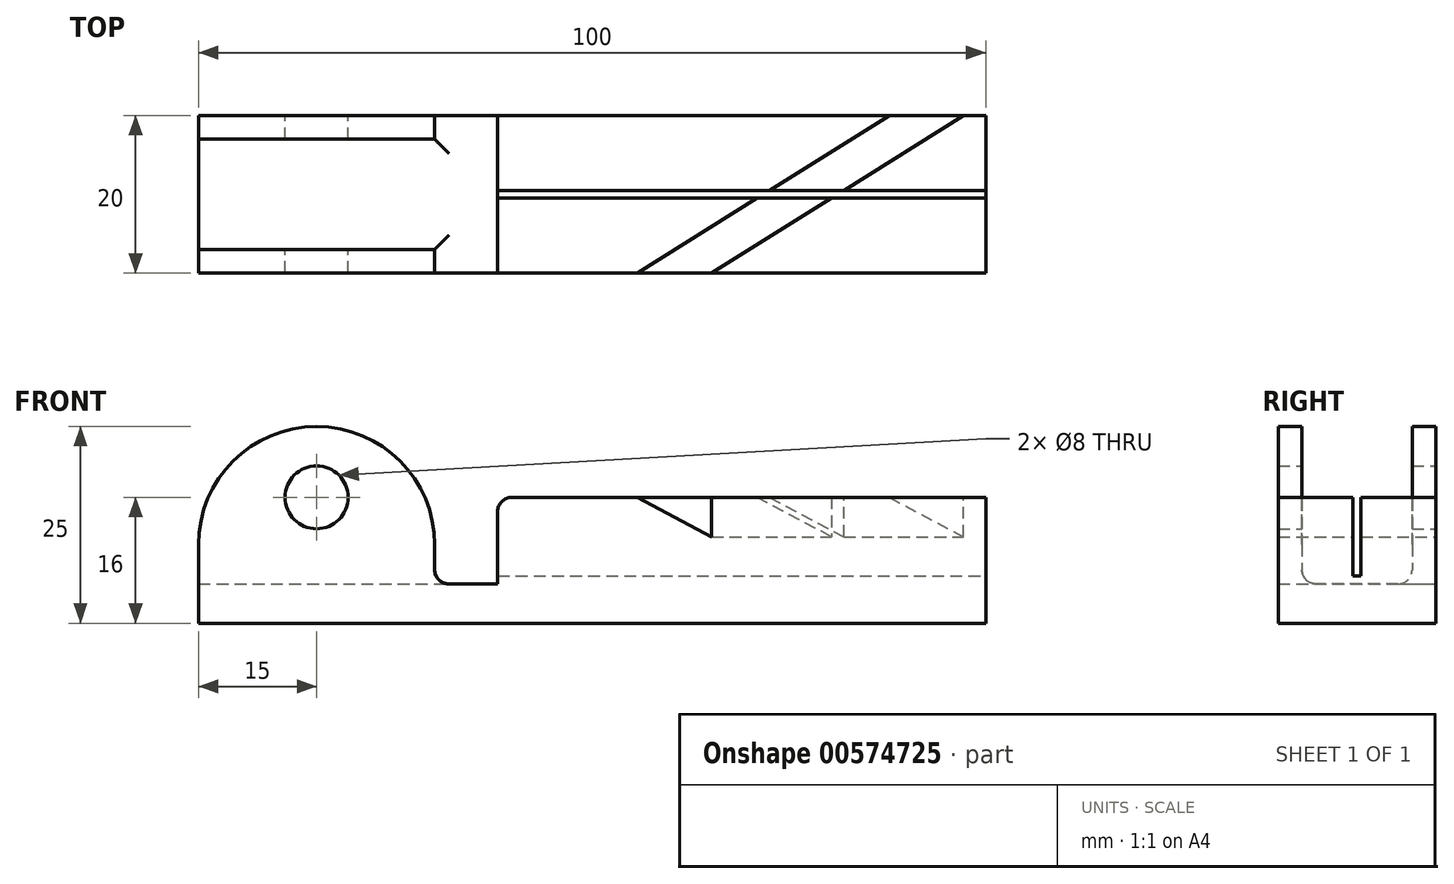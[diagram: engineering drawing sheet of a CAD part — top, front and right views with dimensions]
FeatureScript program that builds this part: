
annotation { "Feature Type Name" : "Feature", "Feature Type Description" : "" }
export const myFeature = defineFeature(function(context is Context, id is Id, definition is map)
    precondition{}
    {
        {
            var Q0;
            Q0=qCreatedBy(makeId("Front.planeOp"),FACE);
            var sketch = newSketch(context, id + "F0", { "sketchPlane" : qUnion([Q0])});
            skLineSegment(sketch, "E0", {"start": v(0, -25) * mm, "end": v(100, -25) * mm});
            skLineSegment(sketch, "E1", {"start": v(100, -25) * mm, "end": v(100, -9) * mm});
            skLineSegment(sketch, "E2", {"start": v(100, -9) * mm, "end": v(38, -9) * mm});
            skLineSegment(sketch, "E3", {"start": v(38, -9) * mm, "end": v(38, -20) * mm});
            skLineSegment(sketch, "E4", {"start": v(38, -20) * mm, "end": v(0, -20) * mm});
            skLineSegment(sketch, "E5", {"start": v(0, -20) * mm, "end": v(0, -25) * mm});
            skLineSegment(sketch, "E6", {"start": v(30, -15) * mm, "end": v(30, -20) * mm});
            skLineSegment(sketch, "E7", {"start": v(0, -15) * mm, "end": v(0, -20) * mm});
            skArc(sketch, "E8.trimOffspring", {"start": v(30, -15) * mm, "mid": v(15, 0) * mm, "end": v(0, -15) * mm});
            skCircle(sketch, "E9", {"center": v(15, -9) * mm, "radius": 4 * mm});
            skSolve(sketch);
        }
        {
            var Q0;
            Q0=makeQuery(id+"F0.imprint","IMPRINT",FACE,{"disambiguationData":[TD([[makeQuery(id+"F0.imprint","IMPRINT",EDGE,{"derivedFrom":sQuery(id+"F0.wireOp",EDGE,"E0")}),1.0]])]});
            var Q1;
            {var subQ1=sQuery(id+"F0.wireOp",EDGE,"E6");Q1=makeQuery(id+"F0.imprint","IMPRINT",FACE,{"disambiguationData":[TD([[makeQuery(id+"F0.imprint","IMPRINT",EDGE,{"derivedFrom":subQ1}),-1.0]])]});}
            extrude(context, id + "F1", {"entities" : qUnion([Q0, Q1]), "endBound" : BoundingType.SYMMETRIC, "depth" : 20 * mm, "offsetDistance" : 25 * mm});
        }
        {
            var Q0;
            Q0=qCreatedBy(makeId("Front.planeOp"),FACE);
            var sketch = newSketch(context, id + "F2", { "sketchPlane" : qUnion([Q0])});
            skArc(sketch, "E10.0", {"start": v(30, -15) * mm, "mid": v(15, 0) * mm, "end": v(0, -15) * mm});
            skLineSegment(sketch, "E10.1", {"start": v(30, -15) * mm, "end": v(30, -20) * mm});
            skPoint(sketch, "E10.2", {"position": v(30, -20) * mm});
            skPoint(sketch, "E10.3", {"position": v(0, -15) * mm});
            skPoint(sketch, "E10.4", {"position": v(0, -20) * mm});
            skLineSegment(sketch, "E11", {"start": v(0, -15) * mm, "end": v(0, -20) * mm});
            skLineSegment(sketch, "E12", {"start": v(0, -20) * mm, "end": v(30, -20) * mm});
            skSolve(sketch);
        }
        {
            var Q0;
            Q0 = qSketchRegion(id + "F2", true);
            extrude(context, id + "F3", {"entities" : qUnion([Q0]), "operationType" : NewBodyOperationType.REMOVE, "endBound" : BoundingType.SYMMETRIC, "oppositeDirection" : true, "depth" : 14 * mm, "offsetDistance" : 25 * mm});
        }
        {
            var Q0;
            Q0=makeQuery(id+"F3.boolean.opBoolean","COPY",EDGE,{"derivedFrom":makeQuery(id+"F3.opExtrude","CAP_EDGE",EDGE,{"disambiguationData":[OSD([sQuery(id+"F2.wireOp",EDGE,"E12")])],"isStart":false})});
            var Q1;
            Q1=makeQuery(id+"F3.boolean.opBoolean","COPY",EDGE,{"derivedFrom":makeQuery(id+"F3.opExtrude","CAP_EDGE",EDGE,{"disambiguationData":[OSD([sQuery(id+"F2.wireOp",EDGE,"E12")])],"isStart":true})});
            var Q2;
            {var subQ0=sQuery(id+"F2.wireOp",EDGE,"E12");var subQ1=sQuery(id+"F0.wireOp",EDGE,"E4");var subQ2=sQuery(id+"F0.wireOp",EDGE,"E6");Q2=makeQuery(id+"F3.boolean.opBoolean","SPLIT",EDGE,{"disambiguationData":[TD([makeQuery(id+"F3.opExtrude","CAP_FACE",FACE,{"disambiguationData":[OSD([sQuery(id+"F2.wireOp",EDGE,"E10.0"),sQuery(id+"F2.wireOp",EDGE,"E10.1"),sQuery(id+"F2.wireOp",EDGE,"E11"),subQ0])],"isStart":true})])],"derivedFrom":makeQuery(id+"F1.opExtrude","SWEPT_EDGE",EDGE,{"disambiguationData":[OSD([subQ1,subQ2])]})});}
            var Q3;
            {var subQ0=sQuery(id+"F0.wireOp",EDGE,"E6");var subQ1=sQuery(id+"F2.wireOp",EDGE,"E12");var subQ2=sQuery(id+"F0.wireOp",EDGE,"E4");Q3=makeQuery(id+"F3.boolean.opBoolean","SPLIT",EDGE,{"disambiguationData":[TD([makeQuery(id+"F3.opExtrude","CAP_FACE",FACE,{"disambiguationData":[OSD([sQuery(id+"F2.wireOp",EDGE,"E10.0"),sQuery(id+"F2.wireOp",EDGE,"E10.1"),sQuery(id+"F2.wireOp",EDGE,"E11"),subQ1])],"isStart":false})])],"derivedFrom":makeQuery(id+"F1.opExtrude","SWEPT_EDGE",EDGE,{"disambiguationData":[OSD([subQ2,subQ0])]})});}
            var Q4;
            Q4=makeQuery(id+"F1.opExtrude","SWEPT_EDGE",EDGE,{"disambiguationData":[OSD([sQuery(id+"F0.wireOp",EDGE,"E2"),sQuery(id+"F0.wireOp",EDGE,"E3")])]});
            fillet(context, id + "F4", {"entities" : qUnion([Q0, Q1, Q2, Q3, Q4]), "radius" : 1.8 * mm, "tangentPropagation" : true, "allowEdgeOverflow" : false});
        }
        {
            var Q0;
            Q0=qCreatedBy(makeId("Right.planeOp"),FACE);
            cPlane(context, id + "F5", {"entities" : qUnion([Q0]), "cplaneType" : CPlaneType.OFFSET, "offset" : 75 * mm, "width" : 150 * mm, "height" : 150 * mm});
        }
        {
            var Q0;
            Q0=qCreatedBy(id+"F5.planeOp",FACE);
            var sketch = newSketch(context, id + "F6", { "sketchPlane" : qUnion([Q0])});
            skLineSegment(sketch, "E13", {"start": v(0, 25.9) * mm, "end": v(0, -59.65) * mm, "construction": true});
            skSolve(sketch);
        }
        {
            var Q0;
            Q0 = qBodyType(qCreatedBy(id + "F6" ,EDGE), BodyType.WIRE);
            cPlane(context, id + "F7", {"entities" : qUnion([Q0]), "cplaneType" : CPlaneType.LINE_ANGLE, "offset" : 25 * mm, "angle" : 148 * degree, "width" : 150 * mm, "height" : 150 * mm});
        }
        {
            var Q0;
            Q0=qCreatedBy(id+"F7.planeOp",FACE);
            var sketch = newSketch(context, id + "F8", { "sketchPlane" : qUnion([Q0])});
            skLineSegment(sketch, "E14", {"start": v(-43.02, -9) * mm, "end": v(-43.02, -14) * mm});
            skLineSegment(sketch, "E15", {"start": v(-43.02, -14) * mm, "end": v(-38.02, -9) * mm});
            skLineSegment(sketch, "E16", {"start": v(-38.02, -9) * mm, "end": v(-43.02, -9) * mm});
            skSolve(sketch);
        }
        {
            var Q0;
            Q0 = qSketchRegion(id + "F8", true);
            extrude(context, id + "F9", {"entities" : qUnion([Q0]), "operationType" : NewBodyOperationType.REMOVE, "endBound" : BoundingType.SYMMETRIC, "oppositeDirection" : true, "depth" : 50 * mm, "offsetDistance" : 25 * mm});
        }
        {
            var Q0;
            Q0=qCreatedBy(id+"F5.planeOp",FACE);
            var sketch = newSketch(context, id + "F10", { "sketchPlane" : qUnion([Q0])});
            skPoint(sketch, "E17.0", {"position": v(0, -9) * mm});
            skLineSegment(sketch, "E18", {"start": v(0, -9) * mm, "end": v(-0.5, -9) * mm});
            skLineSegment(sketch, "E19", {"start": v(-0.5, -9) * mm, "end": v(-0.5, -19) * mm});
            skLineSegment(sketch, "E20", {"start": v(-0.5, -19) * mm, "end": v(0.5, -19) * mm});
            skLineSegment(sketch, "E21", {"start": v(0.5, -19) * mm, "end": v(0.5, -9) * mm});
            skLineSegment(sketch, "E22", {"start": v(0.5, -9) * mm, "end": v(0, -9) * mm});
            skSolve(sketch);
        }
        {
            var Q0;
            Q0 = qSketchRegion(id + "F10", true);
            extrude(context, id + "F11", {"entities" : qUnion([Q0]), "operationType" : NewBodyOperationType.REMOVE, "endBound" : BoundingType.SYMMETRIC, "oppositeDirection" : true, "depth" : 80 * mm, "offsetDistance" : 25 * mm});
        }
    });
